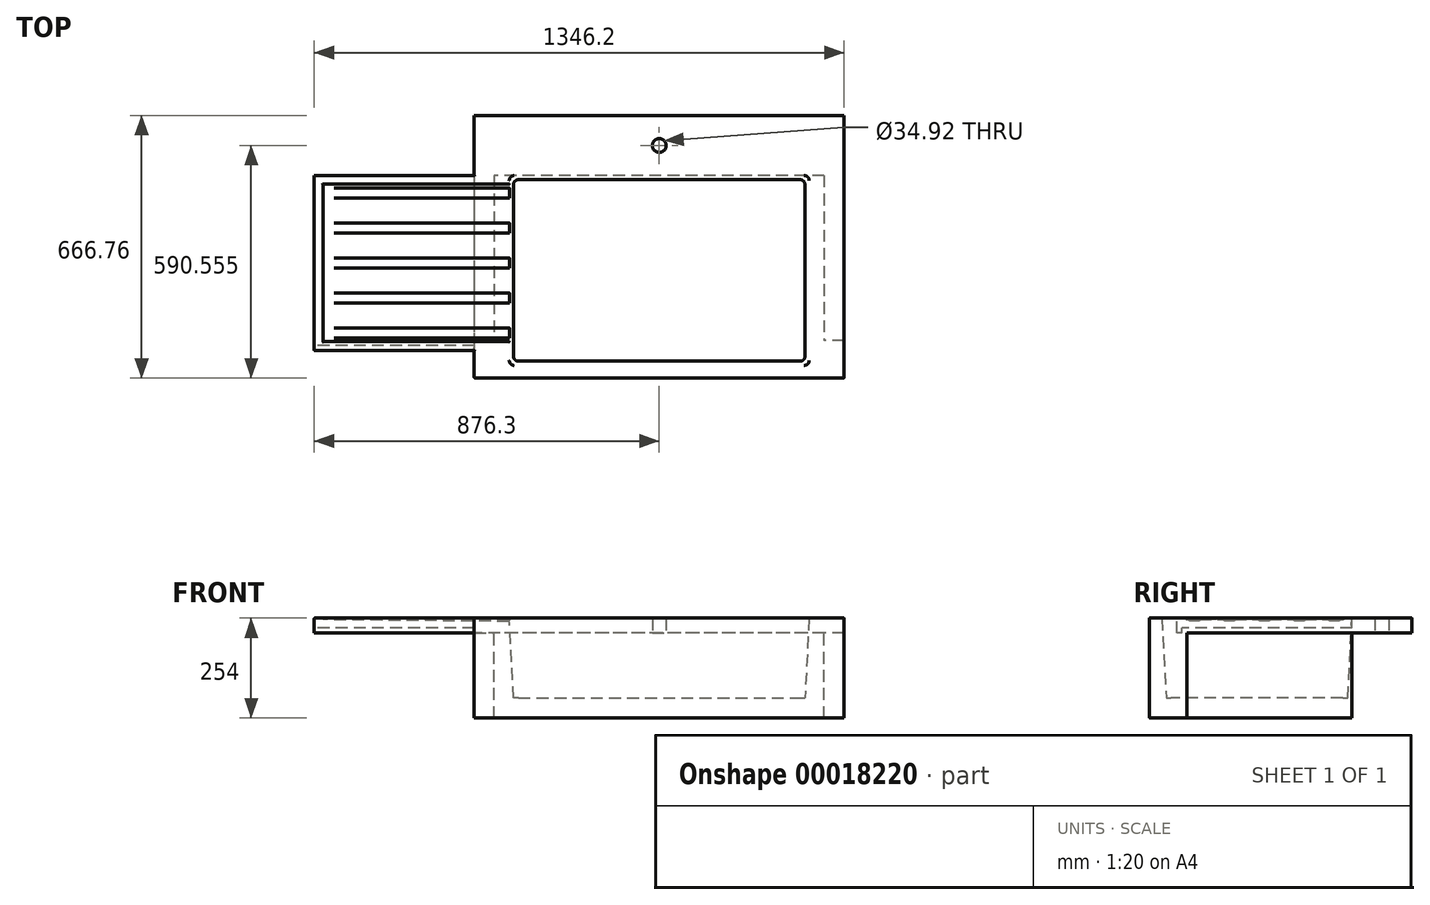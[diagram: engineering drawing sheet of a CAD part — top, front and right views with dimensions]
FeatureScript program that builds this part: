
annotation { "Feature Type Name" : "Feature", "Feature Type Description" : "" }
export const myFeature = defineFeature(function(context is Context, id is Id, definition is map)
    precondition{}
    {
        {
            var Q0;
            Q0=qCreatedBy(makeId("Top.planeOp"),FACE);
            var sketch = newSketch(context, id + "F0", { "sketchPlane" : qUnion([Q0])});
            skLineSegment(sketch, "E0.rect.bottom", {"start": v(419.1, -333.38) * mm, "end": v(-419.1, -333.38) * mm});
            skLineSegment(sketch, "E0.rect.top", {"start": v(419.1, 333.38) * mm, "end": v(-419.1, 333.38) * mm});
            skLineSegment(sketch, "E0.rect.left", {"start": v(419.1, -333.38) * mm, "end": v(419.1, 333.38) * mm});
            skLineSegment(sketch, "E0.rect.right", {"start": v(-419.1, -333.38) * mm, "end": v(-419.1, 333.38) * mm});
            skPoint(sketch, "E0.rect.middle", {"position": v(0, 0) * mm});
            skSolve(sketch);
        }
        {
            var Q0;
            Q0 = qSketchRegion(id + "F0", true);
            extrude(context, id + "F1", {"entities" : qUnion([Q0]), "oppositeDirection" : true, "depth" : 254 * mm});
        }
        {
            var Q0;
            Q0=makeQuery(id+"F1.opExtrude","CAP_FACE",FACE,{"disambiguationData":[OSD([sQuery(id+"F0.wireOp",EDGE,"E0.rect.bottom"),sQuery(id+"F0.wireOp",EDGE,"E0.rect.top"),sQuery(id+"F0.wireOp",EDGE,"E0.rect.left"),sQuery(id+"F0.wireOp",EDGE,"E0.rect.right")])],"isStart":true});
            var sketch = newSketch(context, id + "F2", { "sketchPlane" : qUnion([Q0])});
            skLineSegment(sketch, "E1.rect.bottom", {"start": v(381, -301.63) * mm, "end": v(-381, -301.63) * mm});
            skLineSegment(sketch, "E1.rect.top", {"start": v(381, 180.98) * mm, "end": v(-381, 180.97) * mm});
            skLineSegment(sketch, "E1.rect.left", {"start": v(381, -301.63) * mm, "end": v(381, 180.98) * mm});
            skLineSegment(sketch, "E1.rect.right", {"start": v(-381, -301.63) * mm, "end": v(-381, 180.97) * mm});
            skLineSegment(sketch, "E2.0", {"start": v(419.1, -333.38) * mm, "end": v(-419.1, -333.38) * mm, "construction": true});
            skLineSegment(sketch, "E3.0", {"start": v(419.1, -333.38) * mm, "end": v(419.1, 333.38) * mm, "construction": true});
            skLineSegment(sketch, "E4.0", {"start": v(419.1, 333.38) * mm, "end": v(-419.1, 333.38) * mm, "construction": true});
            skLineSegment(sketch, "E5.0", {"start": v(-419.1, -333.38) * mm, "end": v(-419.1, 333.38) * mm, "construction": true});
            skSolve(sketch);
        }
        {
            var Q0;
            Q0 = qSketchRegion(id + "F2", true);
            extrude(context, id + "F3", {"entities" : qUnion([Q0]), "operationType" : NewBodyOperationType.REMOVE, "oppositeDirection" : true, "depth" : 203.2 * mm, "hasDraft" : true, "draftAngle" : 3 * degree, "draftPullDirection" : true});
        }
        {
            var Q0;
            Q0=makeQuery(id+"F1.opExtrude","CAP_FACE",FACE,{"disambiguationData":[OSD([sQuery(id+"F0.wireOp",EDGE,"E0.rect.bottom"),sQuery(id+"F0.wireOp",EDGE,"E0.rect.top"),sQuery(id+"F0.wireOp",EDGE,"E0.rect.left"),sQuery(id+"F0.wireOp",EDGE,"E0.rect.right")])],"isStart":false});
            var sketch = newSketch(context, id + "F4", { "sketchPlane" : qUnion([Q0])});
            skLineSegment(sketch, "E6.bottom", {"start": v(419.1, -333.38) * mm, "end": v(-419.1, -333.38) * mm});
            skLineSegment(sketch, "E6.top", {"start": v(419.1, -180.98) * mm, "end": v(-419.1, -180.98) * mm});
            skLineSegment(sketch, "E6.left", {"start": v(419.1, -333.38) * mm, "end": v(419.1, -180.98) * mm});
            skLineSegment(sketch, "E6.right", {"start": v(-419.1, -333.38) * mm, "end": v(-419.1, -180.98) * mm});
            skLineSegment(sketch, "E7.0", {"start": v(381, -180.98) * mm, "end": v(-381, -180.97) * mm, "construction": true});
            skSolve(sketch);
        }
        {
            var Q0;
            Q0=makeQuery(id+"F4.imprint","IMPRINT",FACE,{"disambiguationData":[TD([[makeQuery(id+"F4.imprint","IMPRINT",EDGE,{"derivedFrom":sQuery(id+"F4.wireOp",EDGE,"E6.bottom")}),-1.0]])]});
            extrude(context, id + "F5", {"entities" : qUnion([Q0]), "operationType" : NewBodyOperationType.REMOVE, "oppositeDirection" : true, "depth" : 215.9 * mm});
        }
        {
            var Q0;
            Q0=makeQuery(id+"F1.opExtrude","SWEPT_FACE",FACE,{"disambiguationData":[OSD([sQuery(id+"F0.wireOp",EDGE,"E0.rect.bottom")])]});
            var sketch = newSketch(context, id + "F6", { "sketchPlane" : qUnion([Q0])});
            skLineSegment(sketch, "E8.bottom", {"start": v(-419.1, 0) * mm, "end": v(-469.9, 0) * mm});
            skLineSegment(sketch, "E8.top", {"start": v(-419.1, -38.1) * mm, "end": v(-469.9, -38.1) * mm});
            skLineSegment(sketch, "E8.left", {"start": v(-419.1, 0) * mm, "end": v(-419.1, -38.1) * mm});
            skLineSegment(sketch, "E8.right", {"start": v(-469.9, 0) * mm, "end": v(-469.9, -38.1) * mm});
            skLineSegment(sketch, "E9", {"start": v(0, 0) * mm, "end": v(0, -254) * mm, "construction": true});
            skLineSegment(sketch, "E10.MirrorCS", {"start": v(419.1, 0) * mm, "end": v(419.1, -38.1) * mm});
            skLineSegment(sketch, "E11.MirrorCS", {"start": v(469.9, 0) * mm, "end": v(469.9, -38.1) * mm});
            skLineSegment(sketch, "E12.MirrorCS", {"start": v(419.1, 0) * mm, "end": v(469.9, 0) * mm});
            skLineSegment(sketch, "E13.MirrorCS", {"start": v(419.1, -38.1) * mm, "end": v(469.9, -38.1) * mm});
            skSolve(sketch);
        }
        {
            var Q0;
            Q0=makeQuery(id+"F6.imprint","IMPRINT",FACE,{"disambiguationData":[TD([[makeQuery(id+"F6.imprint","IMPRINT",EDGE,{"derivedFrom":sQuery(id+"F6.wireOp",EDGE,"E8.bottom")}),1.0]])]});
            var Q1;
            Q1=makeQuery(id+"F6.imprint","IMPRINT",FACE,{"disambiguationData":[TD([[makeQuery(id+"F6.imprint","IMPRINT",EDGE,{"derivedFrom":sQuery(id+"F6.wireOp",EDGE,"E10.MirrorCS")}),-1.0]])]});
            var Q2;
            Q2=makeQuery(id+"F1.opExtrude","SWEPT_FACE",FACE,{"disambiguationData":[OSD([sQuery(id+"F0.wireOp",EDGE,"E0.rect.top")])]});
            extrude(context, id + "F7", {"entities" : qUnion([Q0, Q1]), "operationType" : NewBodyOperationType.ADD, "endBound" : BoundingType.UP_TO_SURFACE, "oppositeDirection" : true, "endBoundEntityFace" : qUnion([Q2]), "depth" : 25.4 * mm});
        }
        {
            var Q0;
            Q0=makeQuery(id+"F7.boolean.opBoolean","MERGE",FACE,{"derivedFrom":[makeQuery(id+"F5.boolean.opBoolean","COPY",FACE,{"derivedFrom":makeQuery(id+"F5.opExtrude","CAP_FACE",FACE,{"disambiguationData":[OSD([sQuery(id+"F4.wireOp",EDGE,"E6.bottom"),sQuery(id+"F4.wireOp",EDGE,"E6.top"),sQuery(id+"F4.wireOp",EDGE,"E6.left"),sQuery(id+"F4.wireOp",EDGE,"E6.right")])],"isStart":false})}),makeQuery(id+"F7.opExtrude","SWEPT_FACE",FACE,{"disambiguationData":[OSD([sQuery(id+"F6.wireOp",EDGE,"E8.top")])]}),makeQuery(id+"F7.opExtrude","SWEPT_FACE",FACE,{"disambiguationData":[OSD([sQuery(id+"F6.wireOp",EDGE,"E13.MirrorCS")])]})]});
            var sketch = newSketch(context, id + "F8", { "sketchPlane" : qUnion([Q0])});
            skLineSegment(sketch, "E14.bottom", {"start": v(-469.9, 333.38) * mm, "end": v(-419.1, 333.38) * mm});
            skLineSegment(sketch, "E14.top", {"start": v(-469.9, 238.12) * mm, "end": v(-419.1, 238.12) * mm});
            skLineSegment(sketch, "E14.left", {"start": v(-469.9, 333.38) * mm, "end": v(-469.9, 238.12) * mm});
            skLineSegment(sketch, "E14.right", {"start": v(-419.1, 333.38) * mm, "end": v(-419.1, 238.12) * mm});
            skLineSegment(sketch, "E15", {"start": v(0, 0) * mm, "end": v(0, 333.38) * mm, "construction": true});
            skLineSegment(sketch, "E16.MirrorCS", {"start": v(469.9, 333.38) * mm, "end": v(469.9, 238.12) * mm});
            skLineSegment(sketch, "E17.MirrorCS", {"start": v(419.1, 333.38) * mm, "end": v(419.1, 238.12) * mm});
            skLineSegment(sketch, "E18.MirrorCS", {"start": v(469.9, 333.38) * mm, "end": v(419.1, 333.38) * mm});
            skLineSegment(sketch, "E19.MirrorCS", {"start": v(469.9, 238.12) * mm, "end": v(419.1, 238.12) * mm});
            skSolve(sketch);
        }
        {
            var Q0;
            Q0 = qSketchRegion(id + "F8", true);
            var Q1;
            Q1=makeQuery(id+"F1.opExtrude","CAP_FACE",FACE,{"disambiguationData":[OSD([sQuery(id+"F0.wireOp",EDGE,"E0.rect.bottom"),sQuery(id+"F0.wireOp",EDGE,"E0.rect.top"),sQuery(id+"F0.wireOp",EDGE,"E0.rect.left"),sQuery(id+"F0.wireOp",EDGE,"E0.rect.right")])],"isStart":false});
            extrude(context, id + "F9", {"entities" : qUnion([Q0]), "operationType" : NewBodyOperationType.ADD, "endBound" : BoundingType.UP_TO_SURFACE, "endBoundEntityFace" : qUnion([Q1]), "depth" : 25.4 * mm});
        }
        {
            var Q0;
            Q0=makeQuery(id+"F7.boolean.opBoolean","MERGE",FACE,{"derivedFrom":[makeQuery(id+"F1.opExtrude","CAP_FACE",FACE,{"disambiguationData":[OSD([sQuery(id+"F0.wireOp",EDGE,"E0.rect.bottom"),sQuery(id+"F0.wireOp",EDGE,"E0.rect.top"),sQuery(id+"F0.wireOp",EDGE,"E0.rect.left"),sQuery(id+"F0.wireOp",EDGE,"E0.rect.right")])],"isStart":true}),makeQuery(id+"F7.opExtrude","SWEPT_FACE",FACE,{"disambiguationData":[OSD([sQuery(id+"F6.wireOp",EDGE,"E8.bottom")])]}),makeQuery(id+"F7.opExtrude","SWEPT_FACE",FACE,{"disambiguationData":[OSD([sQuery(id+"F6.wireOp",EDGE,"E12.MirrorCS")])]})]});
            var sketch = newSketch(context, id + "F10", { "sketchPlane" : qUnion([Q0])});
            skLineSegment(sketch, "E20.bottom", {"start": v(-469.9, 180.97) * mm, "end": v(-876.3, 180.97) * mm});
            skLineSegment(sketch, "E20.top", {"start": v(-469.9, -263.53) * mm, "end": v(-876.3, -263.53) * mm});
            skLineSegment(sketch, "E20.left", {"start": v(-469.9, 180.97) * mm, "end": v(-469.9, -263.53) * mm});
            skLineSegment(sketch, "E20.right", {"start": v(-876.3, 180.97) * mm, "end": v(-876.3, -263.53) * mm});
            skLineSegment(sketch, "E21", {"start": v(-381, 180.97) * mm, "end": v(-469.9, 180.97) * mm, "construction": true});
            skPoint(sketch, "E22", {"position": v(-469.9, -238.13) * mm});
            skSolve(sketch);
        }
        {
            var Q0;
            Q0=makeQuery(id+"F10.imprint","IMPRINT",FACE,{"disambiguationData":[TD([[makeQuery(id+"F10.imprint","IMPRINT",EDGE,{"derivedFrom":sQuery(id+"F10.wireOp",EDGE,"E20.bottom")}),1.0]])]});
            var Q1;
            Q1=makeQuery(id+"F7.boolean.opBoolean","MERGE",FACE,{"derivedFrom":[makeQuery(id+"F5.boolean.opBoolean","COPY",FACE,{"derivedFrom":makeQuery(id+"F5.opExtrude","CAP_FACE",FACE,{"disambiguationData":[OSD([sQuery(id+"F4.wireOp",EDGE,"E6.bottom"),sQuery(id+"F4.wireOp",EDGE,"E6.top"),sQuery(id+"F4.wireOp",EDGE,"E6.left"),sQuery(id+"F4.wireOp",EDGE,"E6.right")])],"isStart":false})}),makeQuery(id+"F7.opExtrude","SWEPT_FACE",FACE,{"disambiguationData":[OSD([sQuery(id+"F6.wireOp",EDGE,"E8.top")])]}),makeQuery(id+"F7.opExtrude","SWEPT_FACE",FACE,{"disambiguationData":[OSD([sQuery(id+"F6.wireOp",EDGE,"E13.MirrorCS")])]})]});
            extrude(context, id + "F11", {"entities" : qUnion([Q0]), "operationType" : NewBodyOperationType.ADD, "oppositeDirection" : true, "endBoundEntityFace" : qUnion([Q1]), "depth" : 25.4 * mm});
        }
        {
            var Q0;
            Q0=makeQuery(id+"F11.boolean.opBoolean","MERGE",FACE,{"derivedFrom":[makeQuery(id+"F7.boolean.opBoolean","MERGE",FACE,{"derivedFrom":[makeQuery(id+"F1.opExtrude","CAP_FACE",FACE,{"disambiguationData":[OSD([sQuery(id+"F0.wireOp",EDGE,"E0.rect.bottom"),sQuery(id+"F0.wireOp",EDGE,"E0.rect.top"),sQuery(id+"F0.wireOp",EDGE,"E0.rect.left"),sQuery(id+"F0.wireOp",EDGE,"E0.rect.right")])],"isStart":true}),makeQuery(id+"F7.opExtrude","SWEPT_FACE",FACE,{"disambiguationData":[OSD([sQuery(id+"F6.wireOp",EDGE,"E8.bottom")])]}),makeQuery(id+"F7.opExtrude","SWEPT_FACE",FACE,{"disambiguationData":[OSD([sQuery(id+"F6.wireOp",EDGE,"E12.MirrorCS")])]})]}),makeQuery(id+"F11.opExtrude","CAP_FACE",FACE,{"disambiguationData":[OSD([sQuery(id+"F10.wireOp",EDGE,"E20.bottom"),sQuery(id+"F10.wireOp",EDGE,"E20.top"),sQuery(id+"F10.wireOp",EDGE,"E20.left"),sQuery(id+"F10.wireOp",EDGE,"E20.right")])],"isStart":true})]});
            var sketch = newSketch(context, id + "F12", { "sketchPlane" : qUnion([Q0])});
            skLineSegment(sketch, "E23.top", {"start": v(-854.08, -241.3) * mm, "end": v(-370.35, -241.3) * mm});
            skLineSegment(sketch, "E23.right", {"start": v(-370.35, 158.75) * mm, "end": v(-370.35, -241.3) * mm});
            skLineSegment(sketch, "E24", {"start": v(-370.35, -41.28) * mm, "end": v(-876.3, -41.28) * mm, "construction": true});
            skLineSegment(sketch, "E25", {"start": v(-370.35, 158.75) * mm, "end": v(-854.08, 158.75) * mm});
            skLineSegment(sketch, "E26", {"start": v(-854.08, 158.75) * mm, "end": v(-854.08, -241.3) * mm});
            skSolve(sketch);
        }
        {
            var Q0;
            {var subQ5=sQuery(id+"F12.wireOp",EDGE,"E26");Q0=makeQuery(id+"F12.imprint","IMPRINT",FACE,{"disambiguationData":[TD([[makeQuery(id+"F12.imprint","IMPRINT",EDGE,{"derivedFrom":subQ5}),1.0]])]});}
            var Q1;
            {var subQ5=sQuery(id+"F12.wireOp",EDGE,"E23.right");Q1=makeQuery(id+"F12.imprint","IMPRINT",FACE,{"disambiguationData":[TD([[makeQuery(id+"F12.imprint","IMPRINT",EDGE,{"derivedFrom":subQ5}),-1.0]])]});}
            extrude(context, id + "F13", {"entities" : qUnion([Q0, Q1]), "operationType" : NewBodyOperationType.REMOVE, "oppositeDirection" : true, "depth" : 3.17 * mm});
        }
        {
            var Q0;
            Q0=makeQuery(id+"F11.boolean.opBoolean","MERGE",FACE,{"derivedFrom":[makeQuery(id+"F7.boolean.opBoolean","MERGE",FACE,{"derivedFrom":[makeQuery(id+"F1.opExtrude","CAP_FACE",FACE,{"disambiguationData":[OSD([sQuery(id+"F0.wireOp",EDGE,"E0.rect.bottom"),sQuery(id+"F0.wireOp",EDGE,"E0.rect.top"),sQuery(id+"F0.wireOp",EDGE,"E0.rect.left"),sQuery(id+"F0.wireOp",EDGE,"E0.rect.right")])],"isStart":true}),makeQuery(id+"F7.opExtrude","SWEPT_FACE",FACE,{"disambiguationData":[OSD([sQuery(id+"F6.wireOp",EDGE,"E8.bottom")])]}),makeQuery(id+"F7.opExtrude","SWEPT_FACE",FACE,{"disambiguationData":[OSD([sQuery(id+"F6.wireOp",EDGE,"E12.MirrorCS")])]})]}),makeQuery(id+"F11.opExtrude","CAP_FACE",FACE,{"disambiguationData":[OSD([sQuery(id+"F10.wireOp",EDGE,"E20.bottom"),sQuery(id+"F10.wireOp",EDGE,"E20.top"),sQuery(id+"F10.wireOp",EDGE,"E20.left"),sQuery(id+"F10.wireOp",EDGE,"E20.right")])],"isStart":true})]});
            var sketch = newSketch(context, id + "F14", { "sketchPlane" : qUnion([Q0])});
            skLineSegment(sketch, "E27", {"start": v(-469.9, 257.17) * mm, "end": v(469.9, 257.17) * mm, "construction": true});
            skLineSegment(sketch, "E28", {"start": v(0, 180.97) * mm, "end": v(0, 333.37) * mm, "construction": true});
            skPoint(sketch, "E29", {"position": v(0, 257.17) * mm});
            skSolve(sketch);
        }
        {
            var Q0;
            Q0=sQuery(id+"F14.wireOp",VERTEX,"E29");
            var Q1;
            Q1=makeQuery(id+"F1.opExtrude","SWEPT_BODY",BODY,{"disambiguationData":[OSD([sQuery(id+"F0.wireOp",EDGE,"E0.rect.bottom"),sQuery(id+"F0.wireOp",EDGE,"E0.rect.top"),sQuery(id+"F0.wireOp",EDGE,"E0.rect.left"),sQuery(id+"F0.wireOp",EDGE,"E0.rect.right")])]});
            hole(context, id + "F15", {"style" : HoleStyle.SIMPLE, "holeDiameter" : 34.92 * mm, "endStyle" : HoleEndStyle.THROUGH, "locations" : qUnion([Q0]), "scope" : qUnion([Q1])});
        }
        {
            var Q0;
            Q0=makeQuery(id+"F11.boolean.opBoolean","MERGE",FACE,{"derivedFrom":[makeQuery(id+"F7.boolean.opBoolean","MERGE",FACE,{"derivedFrom":[makeQuery(id+"F1.opExtrude","CAP_FACE",FACE,{"disambiguationData":[OSD([sQuery(id+"F0.wireOp",EDGE,"E0.rect.bottom"),sQuery(id+"F0.wireOp",EDGE,"E0.rect.top"),sQuery(id+"F0.wireOp",EDGE,"E0.rect.left"),sQuery(id+"F0.wireOp",EDGE,"E0.rect.right")])],"isStart":true}),makeQuery(id+"F7.opExtrude","SWEPT_FACE",FACE,{"disambiguationData":[OSD([sQuery(id+"F6.wireOp",EDGE,"E8.bottom")])]}),makeQuery(id+"F7.opExtrude","SWEPT_FACE",FACE,{"disambiguationData":[OSD([sQuery(id+"F6.wireOp",EDGE,"E12.MirrorCS")])]})]}),makeQuery(id+"F11.opExtrude","CAP_FACE",FACE,{"disambiguationData":[OSD([sQuery(id+"F10.wireOp",EDGE,"E20.bottom"),sQuery(id+"F10.wireOp",EDGE,"E20.top"),sQuery(id+"F10.wireOp",EDGE,"E20.left"),sQuery(id+"F10.wireOp",EDGE,"E20.right")])],"isStart":true})]});
            var sketch = newSketch(context, id + "F16", { "sketchPlane" : qUnion([Q0])});
            skLineSegment(sketch, "E30", {"start": v(-825.5, 155.57) * mm, "end": v(-825.5, -238.13) * mm, "construction": true});
            skSolve(sketch);
        }
        {
            var Q0;
            Q0=sQuery(id+"F16.wireOp",EDGE,"E30");
            cPlane(context, id + "F17", {"entities" : qUnion([Q0]), "cplaneType" : CPlaneType.LINE_ANGLE, "offset" : 152.4 * mm, "angle" : 359.5 * degree, "width" : 152.4 * mm, "height" : 152.4 * mm});
        }
        {
            var Q0;
            Q0=qCreatedBy(id+"F17.planeOp",FACE);
            var sketch = newSketch(context, id + "F18", { "sketchPlane" : qUnion([Q0])});
            skLineSegment(sketch, "E31.0", {"start": v(-825.47, -149.22) * mm, "end": v(-825.47, 231.78) * mm, "construction": true});
            skLineSegment(sketch, "E32.top", {"start": v(-825.47, 206.38) * mm, "end": v(-368.56, 206.38) * mm});
            skLineSegment(sketch, "E32.left", {"start": v(-825.47, 231.78) * mm, "end": v(-825.47, 206.38) * mm});
            skLineSegment(sketch, "E33.0.0.5", {"start": v(-825.47, -149.22) * mm, "end": v(-368.56, -149.22) * mm});
            skLineSegment(sketch, "E34", {"start": v(-368.56, -149.22) * mm, "end": v(-368.56, 231.78) * mm, "construction": true});
            skLineSegment(sketch, "E35", {"start": v(-825.47, 231.78) * mm, "end": v(-368.56, 231.78) * mm});
            skLineSegment(sketch, "E36", {"start": v(-368.56, 231.78) * mm, "end": v(-368.56, 206.38) * mm});
            skLineSegment(sketch, "E37", {"start": v(-825.47, -149.22) * mm, "end": v(-825.47, -123.82) * mm});
            skLineSegment(sketch, "E38", {"start": v(-825.47, -123.82) * mm, "end": v(-368.56, -123.82) * mm});
            skLineSegment(sketch, "E39", {"start": v(-368.56, -123.82) * mm, "end": v(-368.56, -149.22) * mm});
            skLineSegment(sketch, "E40.bottom", {"start": v(-825.47, 117.48) * mm, "end": v(-368.56, 117.48) * mm});
            skLineSegment(sketch, "E40.top", {"start": v(-825.47, 142.88) * mm, "end": v(-368.56, 142.88) * mm});
            skLineSegment(sketch, "E40.left", {"start": v(-825.47, 117.48) * mm, "end": v(-825.47, 142.88) * mm});
            skLineSegment(sketch, "E40.right", {"start": v(-368.56, 117.48) * mm, "end": v(-368.56, 142.88) * mm});
            skLineSegment(sketch, "E41.bottom", {"start": v(-825.47, 28.58) * mm, "end": v(-368.56, 28.58) * mm});
            skLineSegment(sketch, "E41.top", {"start": v(-825.47, 53.98) * mm, "end": v(-368.56, 53.98) * mm});
            skLineSegment(sketch, "E41.left", {"start": v(-825.47, 28.58) * mm, "end": v(-825.47, 53.98) * mm});
            skLineSegment(sketch, "E41.right", {"start": v(-368.56, 28.58) * mm, "end": v(-368.56, 53.98) * mm});
            skLineSegment(sketch, "E42.bottom", {"start": v(-825.47, -60.32) * mm, "end": v(-368.56, -60.32) * mm});
            skLineSegment(sketch, "E42.top", {"start": v(-825.47, -34.92) * mm, "end": v(-368.56, -34.92) * mm});
            skLineSegment(sketch, "E42.left", {"start": v(-825.47, -60.32) * mm, "end": v(-825.47, -34.92) * mm});
            skLineSegment(sketch, "E42.right", {"start": v(-368.56, -60.32) * mm, "end": v(-368.56, -34.92) * mm});
            skSolve(sketch);
        }
        {
            var Q0;
            Q0 = qSketchRegion(id + "F18", true);
            extrude(context, id + "F19", {"entities" : qUnion([Q0]), "operationType" : NewBodyOperationType.REMOVE, "depth" : 6.35 * mm, "symmetric" : true});
        }
        {
            var Q0;
            Q0=makeQuery(id+"F11.opExtrude","SWEPT_FACE",FACE,{"disambiguationData":[OSD([sQuery(id+"F10.wireOp",EDGE,"E20.right")])]});
            var sketch = newSketch(context, id + "F20", { "sketchPlane" : qUnion([Q0])});
            skLineSegment(sketch, "E43.bottom", {"start": v(263.53, -25.4) * mm, "end": v(250.83, -25.4) * mm});
            skLineSegment(sketch, "E43.top", {"start": v(263.53, -38.1) * mm, "end": v(250.83, -38.1) * mm});
            skLineSegment(sketch, "E43.left", {"start": v(263.53, -25.4) * mm, "end": v(263.53, -38.1) * mm});
            skLineSegment(sketch, "E43.right", {"start": v(250.83, -25.4) * mm, "end": v(250.83, -38.1) * mm});
            skSolve(sketch);
        }
        {
            var Q0;
            Q0=makeQuery(id+"F20.imprint","IMPRINT",FACE,{"disambiguationData":[TD([[makeQuery(id+"F20.imprint","IMPRINT",EDGE,{"derivedFrom":sQuery(id+"F20.wireOp",EDGE,"E43.bottom")}),-1.0]])]});
            var Q1;
            Q1=makeQuery(id+"F9.boolean.opBoolean","MERGE",FACE,{"derivedFrom":[makeQuery(id+"F7.opExtrude","SWEPT_FACE",FACE,{"disambiguationData":[OSD([sQuery(id+"F6.wireOp",EDGE,"E8.right")])]}),makeQuery(id+"F9.opExtrude","SWEPT_FACE",FACE,{"disambiguationData":[OSD([sQuery(id+"F8.wireOp",EDGE,"E14.left")])]})]});
            extrude(context, id + "F21", {"entities" : qUnion([Q0]), "operationType" : NewBodyOperationType.ADD, "endBound" : BoundingType.UP_TO_SURFACE, "oppositeDirection" : true, "endBoundEntityFace" : qUnion([Q1]), "depth" : 25.4 * mm});
        }
        {
            var Q0;
            Q0=makeQuery(id+"F3.boolean.opBoolean","COPY",EDGE,{"derivedFrom":makeQuery(id+"F3.opExtrude","SWEPT_EDGE",EDGE,{"disambiguationData":[OSD([sQuery(id+"F2.wireOp",EDGE,"E1.rect.top"),sQuery(id+"F2.wireOp",EDGE,"E1.rect.right")])]})});
            var Q1;
            Q1=makeQuery(id+"F3.boolean.opBoolean","COPY",EDGE,{"derivedFrom":makeQuery(id+"F3.opExtrude","SWEPT_EDGE",EDGE,{"disambiguationData":[OSD([sQuery(id+"F2.wireOp",EDGE,"E1.rect.top"),sQuery(id+"F2.wireOp",EDGE,"E1.rect.left")])]})});
            var Q2;
            Q2=makeQuery(id+"F3.boolean.opBoolean","COPY",EDGE,{"derivedFrom":makeQuery(id+"F3.opExtrude","SWEPT_EDGE",EDGE,{"disambiguationData":[OSD([sQuery(id+"F2.wireOp",EDGE,"E1.rect.bottom"),sQuery(id+"F2.wireOp",EDGE,"E1.rect.right")])]})});
            var Q3;
            Q3=makeQuery(id+"F3.boolean.opBoolean","COPY",EDGE,{"derivedFrom":makeQuery(id+"F3.opExtrude","SWEPT_EDGE",EDGE,{"disambiguationData":[OSD([sQuery(id+"F2.wireOp",EDGE,"E1.rect.bottom"),sQuery(id+"F2.wireOp",EDGE,"E1.rect.left")])]})});
            fillet(context, id + "F22", {"entities" : qUnion([Q0, Q1, Q2, Q3]), "radius" : 12.7 * mm, "tangentPropagation" : true, "allowEdgeOverflow" : false});
        }
        {
            var Q0;
            Q0=makeQuery(id+"F13.boolean.opBoolean","COPY",EDGE,{"derivedFrom":makeQuery(id+"F13.opExtrude","CAP_EDGE",EDGE,{"disambiguationData":[OSD([sQuery(id+"F12.wireOp",EDGE,"E23.bottom")])],"isStart":false})});
            var Q1;
            Q1=makeQuery(id+"F13.boolean.opBoolean","COPY",EDGE,{"derivedFrom":makeQuery(id+"F13.opExtrude","CAP_EDGE",EDGE,{"disambiguationData":[OSD([sQuery(id+"F12.wireOp",EDGE,"E23.bottom")])],"isStart":true})});
            var Q2;
            Q2=makeQuery(id+"F13.boolean.opBoolean","COPY",EDGE,{"derivedFrom":makeQuery(id+"F13.opExtrude","CAP_EDGE",EDGE,{"disambiguationData":[OSD([sQuery(id+"F12.wireOp",EDGE,"E23.left")])],"isStart":false})});
            var Q3;
            Q3=makeQuery(id+"F13.boolean.opBoolean","COPY",EDGE,{"derivedFrom":makeQuery(id+"F13.opExtrude","CAP_EDGE",EDGE,{"disambiguationData":[OSD([sQuery(id+"F12.wireOp",EDGE,"E23.left")])],"isStart":true})});
            var Q4;
            Q4=makeQuery(id+"F13.boolean.opBoolean","COPY",EDGE,{"derivedFrom":makeQuery(id+"F13.opExtrude","CAP_EDGE",EDGE,{"disambiguationData":[OSD([sQuery(id+"F12.wireOp",EDGE,"E23.top")])],"isStart":false})});
            var Q5;
            Q5=makeQuery(id+"F13.boolean.opBoolean","COPY",EDGE,{"derivedFrom":makeQuery(id+"F13.opExtrude","CAP_EDGE",EDGE,{"disambiguationData":[OSD([sQuery(id+"F12.wireOp",EDGE,"E23.top")])],"isStart":true})});
            var Q6;
            Q6=makeQuery(id+"F13.boolean.opBoolean","INTERSECT",EDGE,{"derivedFrom":[makeQuery(id+"F3.boolean.opBoolean","COPY",FACE,{"derivedFrom":makeQuery(id+"F3.opExtrude","SWEPT_FACE",FACE,{"disambiguationData":[OSD([sQuery(id+"F2.wireOp",EDGE,"E1.rect.right")])]})}),makeQuery(id+"F13.opExtrude","CAP_FACE",FACE,{"disambiguationData":[OSD([sQuery(id+"F12.wireOp",EDGE,"E23.bottom"),sQuery(id+"F12.wireOp",EDGE,"E23.top"),sQuery(id+"F12.wireOp",EDGE,"E23.left"),sQuery(id+"F12.wireOp",EDGE,"E23.right")])],"isStart":false})]});
            var Q7;
            Q7=makeQuery(id+"F11.boolean.opBoolean","MERGE",FACE,{"derivedFrom":[makeQuery(id+"F7.boolean.opBoolean","MERGE",FACE,{"derivedFrom":[makeQuery(id+"F1.opExtrude","CAP_FACE",FACE,{"disambiguationData":[OSD([sQuery(id+"F0.wireOp",EDGE,"E0.rect.bottom"),sQuery(id+"F0.wireOp",EDGE,"E0.rect.top"),sQuery(id+"F0.wireOp",EDGE,"E0.rect.left"),sQuery(id+"F0.wireOp",EDGE,"E0.rect.right")])],"isStart":true}),makeQuery(id+"F7.opExtrude","SWEPT_FACE",FACE,{"disambiguationData":[OSD([sQuery(id+"F6.wireOp",EDGE,"E8.bottom")])]}),makeQuery(id+"F7.opExtrude","SWEPT_FACE",FACE,{"disambiguationData":[OSD([sQuery(id+"F6.wireOp",EDGE,"E12.MirrorCS")])]})]}),makeQuery(id+"F11.opExtrude","CAP_FACE",FACE,{"disambiguationData":[OSD([sQuery(id+"F10.wireOp",EDGE,"E20.bottom"),sQuery(id+"F10.wireOp",EDGE,"E20.top"),sQuery(id+"F10.wireOp",EDGE,"E20.left"),sQuery(id+"F10.wireOp",EDGE,"E20.right")])],"isStart":true})]});
            var Q8;
            Q8=makeQuery(id+"F9.boolean.opBoolean","MERGE",FACE,{"derivedFrom":[makeQuery(id+"F7.boolean.opBoolean","MERGE",FACE,{"derivedFrom":[makeQuery(id+"F1.opExtrude","SWEPT_FACE",FACE,{"disambiguationData":[OSD([sQuery(id+"F0.wireOp",EDGE,"E0.rect.bottom")])]}),makeQuery(id+"F7.opExtrude","CAP_FACE",FACE,{"disambiguationData":[OSD([sQuery(id+"F6.wireOp",EDGE,"E8.bottom"),sQuery(id+"F6.wireOp",EDGE,"E8.top"),sQuery(id+"F6.wireOp",EDGE,"E8.left"),sQuery(id+"F6.wireOp",EDGE,"E8.right")])],"isStart":true}),makeQuery(id+"F7.opExtrude","CAP_FACE",FACE,{"disambiguationData":[OSD([sQuery(id+"F6.wireOp",EDGE,"E10.MirrorCS"),sQuery(id+"F6.wireOp",EDGE,"E11.MirrorCS"),sQuery(id+"F6.wireOp",EDGE,"E12.MirrorCS"),sQuery(id+"F6.wireOp",EDGE,"E13.MirrorCS")])],"isStart":true})]}),makeQuery(id+"F9.opExtrude","SWEPT_FACE",FACE,{"disambiguationData":[OSD([sQuery(id+"F8.wireOp",EDGE,"E14.bottom")])]}),makeQuery(id+"F9.opExtrude","SWEPT_FACE",FACE,{"disambiguationData":[OSD([sQuery(id+"F8.wireOp",EDGE,"E18.MirrorCS")])]})]});
            fillet(context, id + "F23", {"entities" : qUnion([Q0, Q1, Q2, Q3, Q4, Q5, Q6, Q7, Q8]), "radius" : 1.27 * mm, "tangentPropagation" : true, "allowEdgeOverflow" : false});
        }
    });
